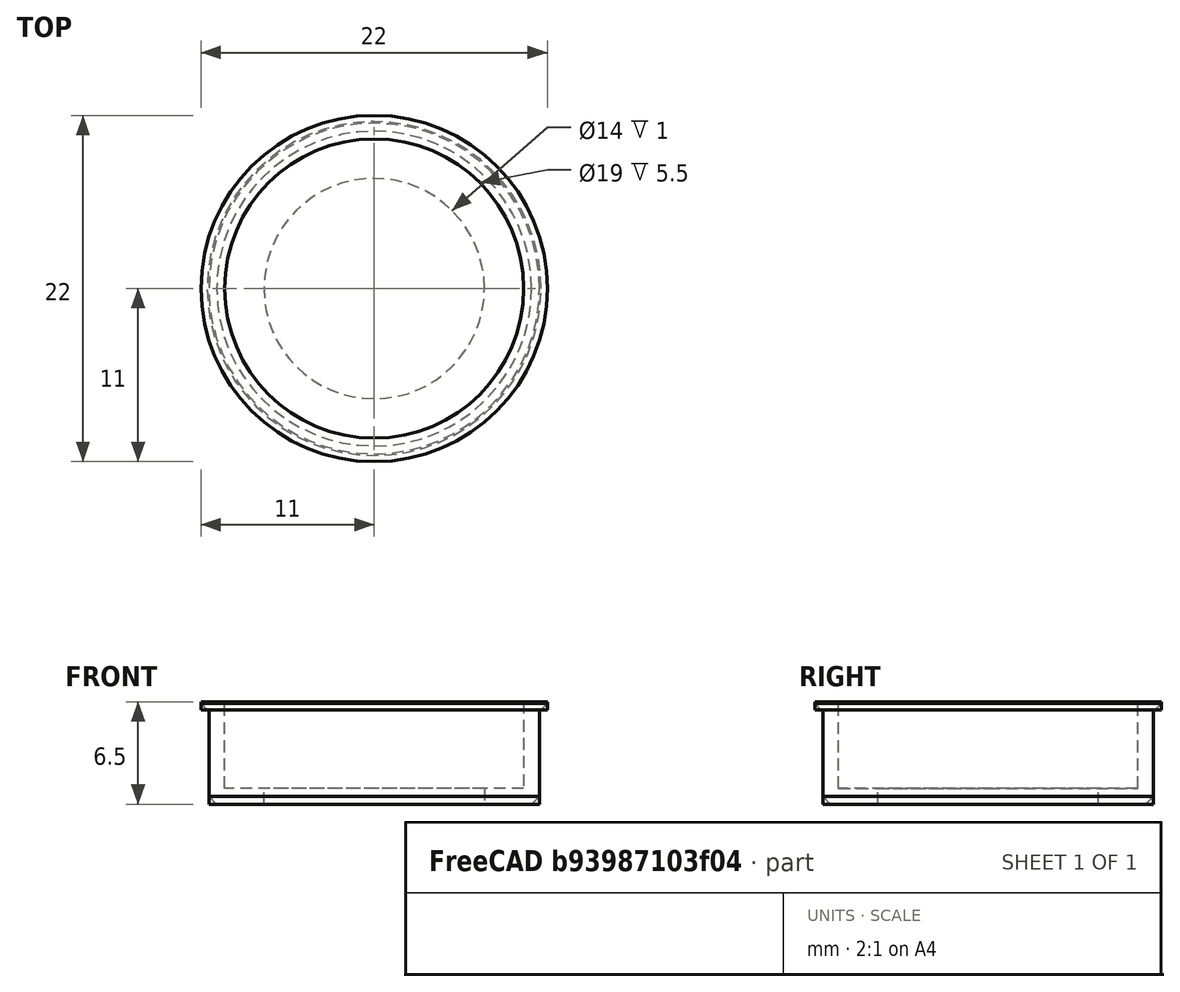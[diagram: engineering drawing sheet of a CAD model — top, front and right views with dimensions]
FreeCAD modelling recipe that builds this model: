
FCSTD DOCUMENT  (FreeCAD 0.16R)
Label: BearingSpacer10mm
License: All rights reserved
LicenseURL: http://en.wikipedia.org/wiki/All_rights_reserved
objects: Sketcher::SketchObject×4, PartDesign::Pad×2, PartDesign::Pocket×2, PartDesign::Chamfer×2, Mesh::Feature×1
note: 14 computed .brp shape members not serialized (recipe doc carries the construction recipe); baked Part::Feature solids carry a one-line shape summary decoded from their .brp

FEATURE [Sketcher::SketchObject] Sketch
  sketch-geometry (1):
    g0: Circle CenterX=0 CenterY=0 CenterZ=0 NormalX=0 NormalY=0 NormalZ=1 Radius=10.5
  constraints (2):
    c: Coincident(g0,g-1)
    c: Radius(g0) = 10.5
FEATURE [PartDesign::Pad] Pad
  Length = 6
  Length2 = 100
  Sketch = -> Sketch
  Type = 0
FEATURE [Sketcher::SketchObject] Sketch001
  Placement = pos=(0,0,6) rot=(0,0,1;0rad)
  Support = -> Pad [Face3]
  sketch-geometry (1):
    g0: Circle CenterX=0 CenterY=0 CenterZ=0 NormalX=0 NormalY=0 NormalZ=1 Radius=11
  constraints (2):
    c: Coincident(g0,g-1)
    c: Radius(g0) = 11
FEATURE [PartDesign::Pad] Pad001
  Length = 0.5
  Length2 = 100
  Sketch = -> Sketch001
  Type = 0
FEATURE [Sketcher::SketchObject] Sketch002
  Placement = pos=(0,0,6.5) rot=(0,0,1;0rad)
  Support = -> Pad001 [Face5]
  sketch-geometry (1):
    g0: Circle CenterX=0 CenterY=0 CenterZ=0 NormalX=0 NormalY=0 NormalZ=1 Radius=9.5
  constraints (2):
    c: Coincident(g0,g-1)
    c: Radius(g0) = 9.5
FEATURE [PartDesign::Pocket] Pocket
  Length = 5.5
  Sketch = -> Sketch002
  Type = 0
FEATURE [Sketcher::SketchObject] Sketch003
  Placement = pos=(0,0,1) rot=(0,0,1;0rad)
  Support = -> Pocket [Face7]
  sketch-geometry (1):
    g0: Circle CenterX=0 CenterY=0 CenterZ=0 NormalX=0 NormalY=0 NormalZ=1 Radius=7
  constraints (2):
    c: Coincident(g0,g-1)
    c: Radius(g0) = 7
FEATURE [PartDesign::Pocket] Pocket001
  Length = 5
  Sketch = -> Sketch003
  Type = 0
FEATURE [PartDesign::Chamfer] Chamfer
  Base = -> Pocket001 [Edge7]
  Size = 0.4
FEATURE [PartDesign::Chamfer] Chamfer001
  Base = -> Chamfer [Edge5]
  Size = 0.5
FEATURE [Mesh::Feature] Mesh  label="Chamfer001 (Meshed)"
